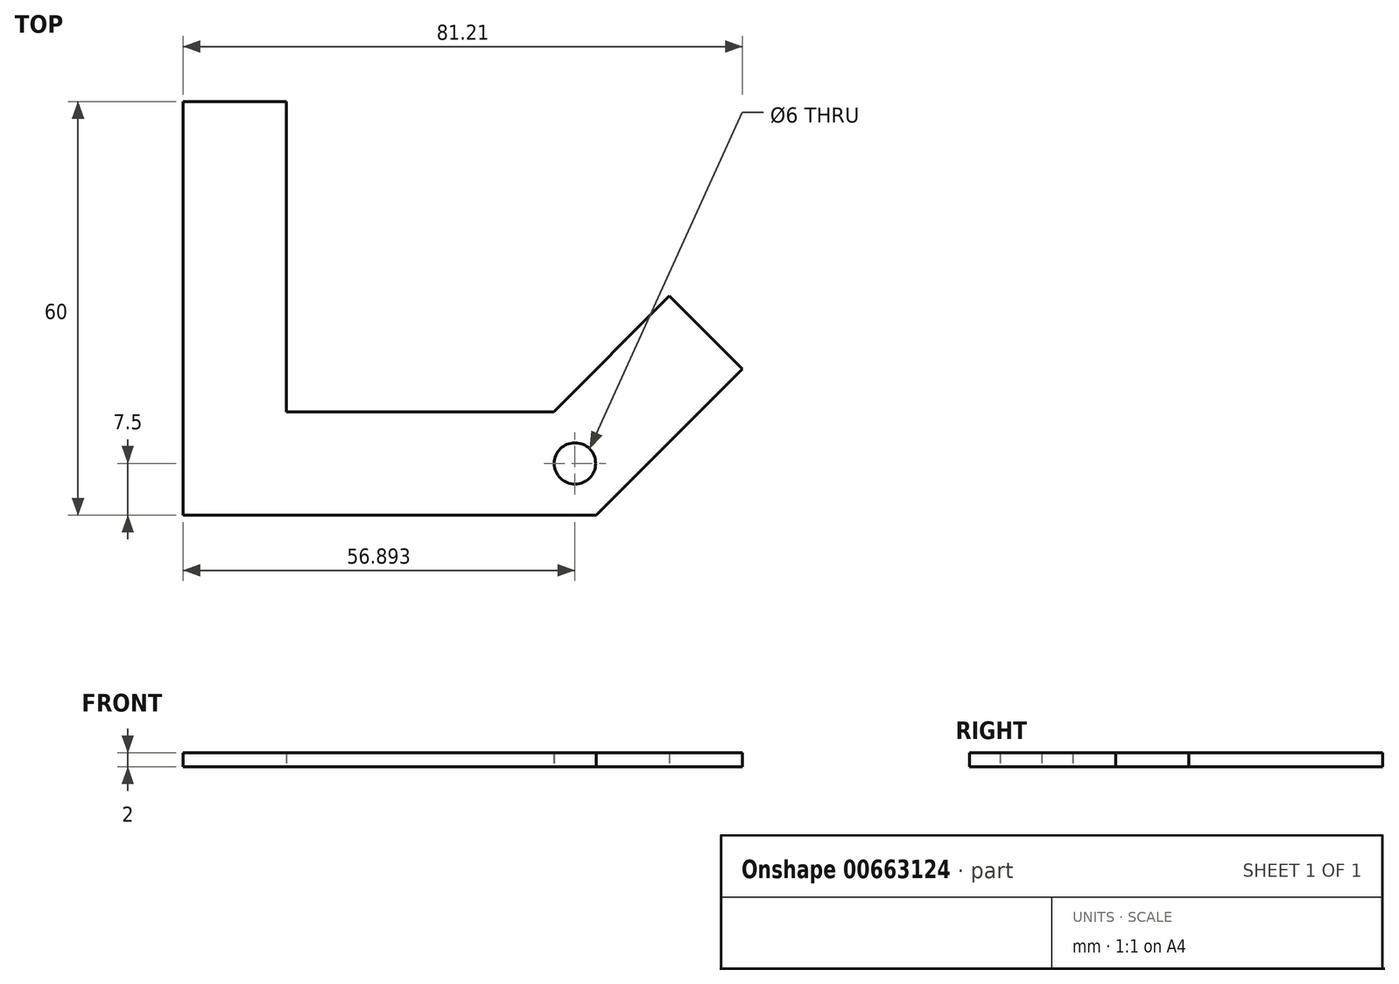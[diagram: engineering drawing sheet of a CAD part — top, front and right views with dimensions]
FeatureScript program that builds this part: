
annotation { "Feature Type Name" : "Feature", "Feature Type Description" : "" }
export const myFeature = defineFeature(function(context is Context, id is Id, definition is map)
    precondition{}
    {
        {
            var Q0;
            Q0=qCreatedBy(makeId("Top.planeOp"),FACE);
            var sketch = newSketch(context, id + "F0", { "sketchPlane" : qUnion([Q0])});
            skLineSegment(sketch, "E0", {"start": v(0, 60) * mm, "end": v(0, 0) * mm});
            skLineSegment(sketch, "E1", {"start": v(0, 0) * mm, "end": v(60, 0) * mm});
            skLineSegment(sketch, "E2", {"start": v(53.79, 15) * mm, "end": v(15, 15) * mm});
            skLineSegment(sketch, "E3", {"start": v(15, 15) * mm, "end": v(15, 60) * mm});
            skLineSegment(sketch, "E4", {"start": v(15, 60) * mm, "end": v(0, 60) * mm});
            skLineSegment(sketch, "E5", {"start": v(60, 0) * mm, "end": v(81.21, 21.21) * mm});
            skLineSegment(sketch, "E6", {"start": v(81.21, 21.21) * mm, "end": v(70.6, 31.82) * mm});
            skLineSegment(sketch, "E7", {"start": v(70.6, 31.82) * mm, "end": v(53.79, 15) * mm});
            skLineSegment(sketch, "E8", {"start": v(53.79, 15) * mm, "end": v(60, 0) * mm, "construction": true});
            skCircle(sketch, "E9", {"center": v(56.9, 7.5) * mm, "radius": 3 * mm});
            skSolve(sketch);
        }
        {
            var Q0;
            Q0 = qSketchRegion(id + "F0", true);
            extrude(context, id + "F1", {"entities" : qUnion([Q0]), "depth" : 2 * mm, "offsetDistance" : 25 * mm});
        }
    });
